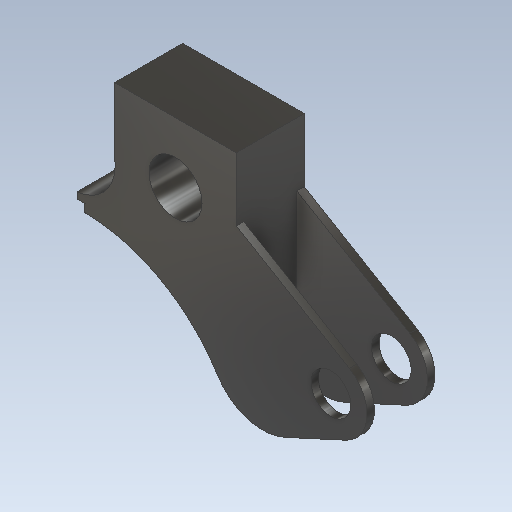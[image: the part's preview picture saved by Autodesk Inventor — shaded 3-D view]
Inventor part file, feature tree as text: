
AUTODESK INVENTOR PART (.ipt)
format: ipt  version: 2021 (Build 250183000, 183)  size: 165,376 bytes
history: native  units: in
note: dims shown in document units (in); Inventor stores cm internally (conversion verified against a paired STEP export)
features: extrude x2, plane x1, fillet x1, sketch x1
ambient origin geometry x8: Origin, YZ Plane, XZ Plane, XY Plane, X Axis, Y Axis, Z Axis, Center Point
bodies: Body1 (feature_tree)
feature tree (5):
  extrude  "Extrusion2"  Depth=0.0787in
  plane  "Work Plane3"
  extrude  "Extrusion6"  Depth=0.0787in
  fillet  "Fillet3"  Radius=0.1803in
  sketch  "Sketch1"  dims[d0=0.7874in d1=0.5146in d7=0.0787in d8=0.1803in d11=0.0591in d12=0.1008in d13=0.0in d29=0.0394in d30=0.0394in d31=0.2062in d32=0.0in d33=0.0787in d34=0.0091in d35=0.0118in]
